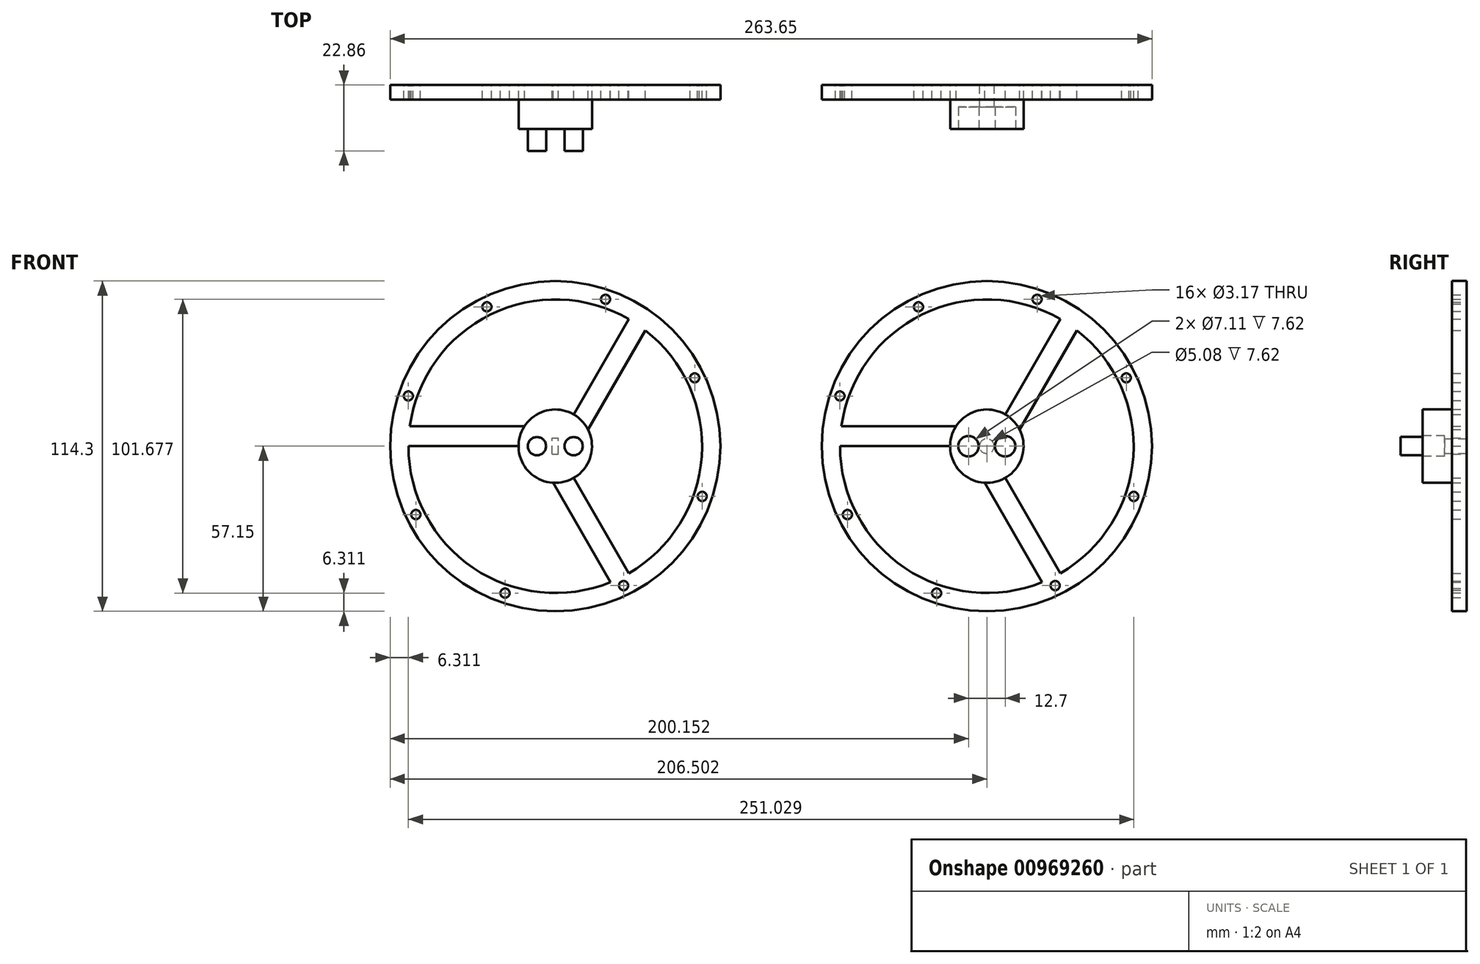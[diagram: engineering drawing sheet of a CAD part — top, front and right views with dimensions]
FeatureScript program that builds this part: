
annotation { "Feature Type Name" : "Feature", "Feature Type Description" : "" }
export const myFeature = defineFeature(function(context is Context, id is Id, definition is map)
    precondition{}
    {
        {
            var Q0;
            Q0=qCreatedBy(makeId("Front.planeOp"),FACE);
            var sketch = newSketch(context, id + "F0", { "sketchPlane" : qUnion([Q0])});
            skCircle(sketch, "E0", {"center": v(0, 0) * mm, "radius": 50.8 * mm});
            skCircle(sketch, "E1", {"center": v(0, 0) * mm, "radius": 57.15 * mm});
            skCircle(sketch, "E2", {"center": v(0, 0) * mm, "radius": 12.7 * mm});
            skLineSegment(sketch, "E3", {"start": v(-50.8, 0) * mm, "end": v(0, 0) * mm});
            skLineSegment(sketch, "E4.bottom", {"start": v(0, 0) * mm, "end": v(-53.72, 0) * mm});
            skLineSegment(sketch, "E4.top", {"start": v(0, 6.97) * mm, "end": v(-53.72, 6.97) * mm});
            skLineSegment(sketch, "E4.left", {"start": v(0, 0) * mm, "end": v(0, 6.97) * mm});
            skLineSegment(sketch, "E4.right", {"start": v(-53.72, 0) * mm, "end": v(-53.72, 6.97) * mm});
            skLineSegment(sketch, "E5.1.0", {"start": v(0, 0) * mm, "end": v(-6.03, -3.48) * mm});
            skLineSegment(sketch, "E5.1.1", {"start": v(-6.03, -3.48) * mm, "end": v(20.83, -50) * mm});
            skLineSegment(sketch, "E5.1.2", {"start": v(0, 0) * mm, "end": v(26.86, -46.52) * mm});
            skLineSegment(sketch, "E5.1.3", {"start": v(26.86, -46.52) * mm, "end": v(20.83, -50) * mm});
            skLineSegment(sketch, "E5.2.0", {"start": v(0, 0) * mm, "end": v(6.03, -3.48) * mm});
            skLineSegment(sketch, "E5.2.1", {"start": v(6.03, -3.48) * mm, "end": v(32.9, 43.04) * mm});
            skLineSegment(sketch, "E5.2.2", {"start": v(0, 0) * mm, "end": v(26.86, 46.52) * mm});
            skLineSegment(sketch, "E5.2.3", {"start": v(26.86, 46.52) * mm, "end": v(32.9, 43.04) * mm});
            skSolve(sketch);
        }
        {
            var Q0;
            {var subQ5=sQuery(id+"F0.wireOp",EDGE,"E4.left");Q0=makeQuery(id+"F0.imprint","IMPRINT",FACE,{"disambiguationData":[TD([[makeQuery(id+"F0.imprint","IMPRINT",EDGE,{"derivedFrom":subQ5}),1.0]])]});}
            var Q1;
            {var subQ5=sQuery(id+"F0.wireOp",EDGE,"E4.left");Q1=makeQuery(id+"F0.imprint","IMPRINT",FACE,{"disambiguationData":[TD([[makeQuery(id+"F0.imprint","IMPRINT",EDGE,{"derivedFrom":subQ5}),-1.0]])]});}
            var Q2;
            {var subQ5=sQuery(id+"F0.wireOp",EDGE,"E5.2.0");Q2=makeQuery(id+"F0.imprint","IMPRINT",FACE,{"disambiguationData":[TD([[makeQuery(id+"F0.imprint","IMPRINT",EDGE,{"derivedFrom":subQ5}),1.0]])]});}
            var Q3;
            {var subQ0=sQuery(id+"F0.wireOp",EDGE,"E5.2.2");var subQ1=sQuery(id+"F0.wireOp",EDGE,"E0");var subQ2=makeQuery(id+"F0.imprint","INTERSECT",VERTEX,{"derivedFrom":[subQ1,subQ0]});Q3=makeQuery(id+"F0.imprint","IMPRINT",FACE,{"disambiguationData":[TD([[makeQuery(id+"F0.imprint","IMPRINT",EDGE,{"disambiguationData":[TD([[subQ2,1.0]])],"derivedFrom":subQ1}),1.0]])]});}
            var Q4;
            {var subQ5=sQuery(id+"F0.wireOp",EDGE,"E5.2.0");Q4=makeQuery(id+"F0.imprint","IMPRINT",FACE,{"disambiguationData":[TD([[makeQuery(id+"F0.imprint","IMPRINT",EDGE,{"derivedFrom":subQ5}),-1.0]])]});}
            var Q5;
            {var subQ5=sQuery(id+"F0.wireOp",EDGE,"E5.1.0");Q5=makeQuery(id+"F0.imprint","IMPRINT",FACE,{"disambiguationData":[TD([[makeQuery(id+"F0.imprint","IMPRINT",EDGE,{"derivedFrom":subQ5}),1.0]])]});}
            var Q6;
            {var subQ5=sQuery(id+"F0.wireOp",EDGE,"E5.1.0");Q6=makeQuery(id+"F0.imprint","IMPRINT",FACE,{"disambiguationData":[TD([[makeQuery(id+"F0.imprint","IMPRINT",EDGE,{"derivedFrom":subQ5}),-1.0]])]});}
            var Q7;
            {var subQ0=sQuery(id+"F0.wireOp",EDGE,"E5.1.1");var subQ1=sQuery(id+"F0.wireOp",EDGE,"E0");var subQ2=makeQuery(id+"F0.imprint","INTERSECT",VERTEX,{"derivedFrom":[subQ1,subQ0]});Q7=makeQuery(id+"F0.imprint","IMPRINT",FACE,{"disambiguationData":[TD([[makeQuery(id+"F0.imprint","IMPRINT",EDGE,{"disambiguationData":[TD([[subQ2,-1.0]])],"derivedFrom":subQ1}),1.0]])]});}
            var Q8;
            {var subQ0=sQuery(id+"F0.wireOp",EDGE,"E4.top");var subQ1=sQuery(id+"F0.wireOp",EDGE,"E0");var subQ2=makeQuery(id+"F0.imprint","INTERSECT",VERTEX,{"derivedFrom":[subQ1,subQ0]});Q8=makeQuery(id+"F0.imprint","IMPRINT",FACE,{"disambiguationData":[TD([[makeQuery(id+"F0.imprint","IMPRINT",EDGE,{"disambiguationData":[TD([[subQ2,-1.0]])],"derivedFrom":subQ1}),1.0]])]});}
            var Q9;
            {var subQ5=sQuery(id+"F0.wireOp",EDGE,"E5.2.3");Q9=makeQuery(id+"F0.imprint","IMPRINT",FACE,{"disambiguationData":[TD([[makeQuery(id+"F0.imprint","IMPRINT",EDGE,{"derivedFrom":subQ5}),-1.0]])]});}
            var Q10;
            {var subQ5=sQuery(id+"F0.wireOp",EDGE,"E5.1.3");Q10=makeQuery(id+"F0.imprint","IMPRINT",FACE,{"disambiguationData":[TD([[makeQuery(id+"F0.imprint","IMPRINT",EDGE,{"derivedFrom":subQ5}),-1.0]])]});}
            var Q11;
            {var subQ5=sQuery(id+"F0.wireOp",EDGE,"E4.right");Q11=makeQuery(id+"F0.imprint","IMPRINT",FACE,{"disambiguationData":[TD([[makeQuery(id+"F0.imprint","IMPRINT",EDGE,{"derivedFrom":subQ5}),-1.0]])]});}
            var Q12;
            Q12=makeQuery(id+"F0.imprint","IMPRINT",FACE,{"disambiguationData":[TD([[makeQuery(id+"F0.imprint","IMPRINT",EDGE,{"derivedFrom":sQuery(id+"F0.wireOp",EDGE,"E1")}),1.0]])]});
            extrude(context, id + "F1", {"entities" : qUnion([Q0, Q1, Q2, Q3, Q4, Q5, Q6, Q7, Q8, Q9, Q10, Q11, Q12]), "depth" : 5.08 * mm, "offsetDistance" : 25.4 * mm});
        }
        {
            var Q0;
            Q0=makeQuery(id+"F1.opExtrude","CAP_FACE",FACE,{"disambiguationData":[OSD([sQuery(id+"F0.wireOp",EDGE,"E0"),sQuery(id+"F0.wireOp",EDGE,"E1"),sQuery(id+"F0.wireOp",EDGE,"E2"),sQuery(id+"F0.wireOp",EDGE,"E4.bottom"),sQuery(id+"F0.wireOp",EDGE,"E4.top"),sQuery(id+"F0.wireOp",EDGE,"E5.1.1"),sQuery(id+"F0.wireOp",EDGE,"E5.1.2"),sQuery(id+"F0.wireOp",EDGE,"E5.2.1"),sQuery(id+"F0.wireOp",EDGE,"E5.2.2")])],"isStart":false});
            var sketch = newSketch(context, id + "F2", { "sketchPlane" : qUnion([Q0])});
            skCircle(sketch, "E6", {"center": v(0, 0) * mm, "radius": 12.7 * mm});
            skSolve(sketch);
        }
        {
            var Q0;
            {var subQ0=sQuery(id+"F2.wireOp",EDGE,"E6");var subQ4=makeQuery(id+"F2.imprint","INTERSECT",VERTEX,{"derivedFrom":[makeQuery(id+"F1.opExtrude","CAP_EDGE",EDGE,{"disambiguationData":[OSD([sQuery(id+"F0.wireOp",EDGE,"E5.2.2")])],"isStart":false}),subQ0]});Q0=makeQuery(id+"F2.imprint","IMPRINT",FACE,{"disambiguationData":[TD([[makeQuery(id+"F2.imprint","IMPRINT",EDGE,{"disambiguationData":[TD([[subQ4,1.0]])],"derivedFrom":subQ0}),1.0]])]});}
            extrude(context, id + "F3", {"entities" : qUnion([Q0]), "operationType" : NewBodyOperationType.ADD, "depth" : 10.16 * mm, "offsetDistance" : 25.4 * mm});
        }
        {
            var Q0;
            Q0=makeQuery(id+"F1.opExtrude","CAP_FACE",FACE,{"disambiguationData":[OSD([sQuery(id+"F0.wireOp",EDGE,"E0"),sQuery(id+"F0.wireOp",EDGE,"E1"),sQuery(id+"F0.wireOp",EDGE,"E2"),sQuery(id+"F0.wireOp",EDGE,"E4.bottom"),sQuery(id+"F0.wireOp",EDGE,"E4.top"),sQuery(id+"F0.wireOp",EDGE,"E5.1.1"),sQuery(id+"F0.wireOp",EDGE,"E5.1.2"),sQuery(id+"F0.wireOp",EDGE,"E5.2.1"),sQuery(id+"F0.wireOp",EDGE,"E5.2.2")])],"isStart":true});
            var sketch = newSketch(context, id + "F4", { "sketchPlane" : qUnion([Q0])});
            skCircle(sketch, "E7", {"center": v(-23.65, -48.24) * mm, "radius": 1.59 * mm});
            skCircle(sketch, "E8.1.0", {"center": v(17.39, -50.84) * mm, "radius": 1.59 * mm});
            skCircle(sketch, "E8.2.0", {"center": v(48.24, -23.65) * mm, "radius": 1.59 * mm});
            skCircle(sketch, "E8.3.0", {"center": v(50.84, 17.39) * mm, "radius": 1.59 * mm});
            skCircle(sketch, "E8.4.0", {"center": v(23.65, 48.24) * mm, "radius": 1.59 * mm});
            skCircle(sketch, "E8.5.0", {"center": v(-17.39, 50.84) * mm, "radius": 1.59 * mm});
            skCircle(sketch, "E8.6.0", {"center": v(-48.24, 23.65) * mm, "radius": 1.59 * mm});
            skCircle(sketch, "E8.7.0", {"center": v(-50.84, -17.39) * mm, "radius": 1.59 * mm});
            skPoint(sketch, "E8.center", {"position": v(0, 0) * mm});
            skSolve(sketch);
        }
        {
            var Q0;
            Q0=makeQuery(id+"F4.imprint","IMPRINT",FACE,{"disambiguationData":[TD([[makeQuery(id+"F4.imprint","IMPRINT",EDGE,{"derivedFrom":sQuery(id+"F4.wireOp",EDGE,"E7")}),1.0]])]});
            var Q1;
            Q1=makeQuery(id+"F4.imprint","IMPRINT",FACE,{"disambiguationData":[TD([[makeQuery(id+"F4.imprint","IMPRINT",EDGE,{"derivedFrom":sQuery(id+"F4.wireOp",EDGE,"E8.7.0")}),1.0]])]});
            var Q2;
            Q2=makeQuery(id+"F4.imprint","IMPRINT",FACE,{"disambiguationData":[TD([[makeQuery(id+"F4.imprint","IMPRINT",EDGE,{"derivedFrom":sQuery(id+"F4.wireOp",EDGE,"E8.6.0")}),1.0]])]});
            var Q3;
            Q3=makeQuery(id+"F4.imprint","IMPRINT",FACE,{"disambiguationData":[TD([[makeQuery(id+"F4.imprint","IMPRINT",EDGE,{"derivedFrom":sQuery(id+"F4.wireOp",EDGE,"E8.5.0")}),1.0]])]});
            var Q4;
            Q4=makeQuery(id+"F4.imprint","IMPRINT",FACE,{"disambiguationData":[TD([[makeQuery(id+"F4.imprint","IMPRINT",EDGE,{"derivedFrom":sQuery(id+"F4.wireOp",EDGE,"E8.4.0")}),1.0]])]});
            var Q5;
            Q5=makeQuery(id+"F4.imprint","IMPRINT",FACE,{"disambiguationData":[TD([[makeQuery(id+"F4.imprint","IMPRINT",EDGE,{"derivedFrom":sQuery(id+"F4.wireOp",EDGE,"E8.3.0")}),1.0]])]});
            var Q6;
            Q6=makeQuery(id+"F4.imprint","IMPRINT",FACE,{"disambiguationData":[TD([[makeQuery(id+"F4.imprint","IMPRINT",EDGE,{"derivedFrom":sQuery(id+"F4.wireOp",EDGE,"E8.2.0")}),1.0]])]});
            var Q7;
            Q7=makeQuery(id+"F4.imprint","IMPRINT",FACE,{"disambiguationData":[TD([[makeQuery(id+"F4.imprint","IMPRINT",EDGE,{"derivedFrom":sQuery(id+"F4.wireOp",EDGE,"E8.1.0")}),1.0]])]});
            extrude(context, id + "F5", {"entities" : qUnion([Q0, Q1, Q2, Q3, Q4, Q5, Q6, Q7]), "operationType" : NewBodyOperationType.REMOVE, "oppositeDirection" : true, "depth" : 25.4 * mm, "offsetDistance" : 25.4 * mm});
        }
        {
            var Q0;
            Q0=makeQuery(id+"F3.opExtrude","CAP_FACE",FACE,{"disambiguationData":[OSD([sQuery(id+"F2.wireOp",EDGE,"E6")])],"isStart":false});
            var sketch = newSketch(context, id + "F6", { "sketchPlane" : qUnion([Q0])});
            skPoint(sketch, "E9.center", {"position": v(0, 0) * mm});
            skLineSegment(sketch, "E10", {"start": v(0, 0) * mm, "end": v(6.35, 0) * mm});
            skCircle(sketch, "E11", {"center": v(6.35, 0) * mm, "radius": 3.18 * mm});
            skCircle(sketch, "E12.1.1", {"center": v(-6.35, 0) * mm, "radius": 3.17 * mm});
            skSolve(sketch);
        }
        {
            var Q0;
            Q0=makeQuery(id+"F1.opExtrude","SWEPT_BODY",BODY,{"disambiguationData":[OSD([sQuery(id+"F0.wireOp",EDGE,"E0"),sQuery(id+"F0.wireOp",EDGE,"E1"),sQuery(id+"F0.wireOp",EDGE,"E2"),sQuery(id+"F0.wireOp",EDGE,"E4.bottom"),sQuery(id+"F0.wireOp",EDGE,"E4.top"),sQuery(id+"F0.wireOp",EDGE,"E5.1.1"),sQuery(id+"F0.wireOp",EDGE,"E5.1.2"),sQuery(id+"F0.wireOp",EDGE,"E5.2.1"),sQuery(id+"F0.wireOp",EDGE,"E5.2.2")])]});
            transform(context, id + "F7", {"entities" : qUnion([Q0]), "transformType" : TransformType.TRANSLATION_3D, "dx" : 177.3 * mm, "dy" : 0 * mm, "dz" : 0 * mm, "makeCopy" : true});
        }
        {
            var Q0;
            Q0=makeQuery(id+"F6.imprint","IMPRINT",FACE,{"disambiguationData":[TD([[makeQuery(id+"F6.imprint","IMPRINT",EDGE,{"derivedFrom":sQuery(id+"F6.wireOp",EDGE,"E12.1.1")}),1.0]])]});
            var Q1;
            Q1=makeQuery(id+"F6.imprint","IMPRINT",FACE,{"disambiguationData":[TD([[makeQuery(id+"F6.imprint","IMPRINT",EDGE,{"derivedFrom":sQuery(id+"F6.wireOp",EDGE,"E12.2.1")}),1.0]])]});
            var Q2;
            Q2=makeQuery(id+"F6.imprint","IMPRINT",FACE,{"disambiguationData":[TD([[makeQuery(id+"F6.imprint","IMPRINT",EDGE,{"derivedFrom":sQuery(id+"F6.wireOp",EDGE,"E11")}),1.0]])]});
            extrude(context, id + "F8", {"entities" : qUnion([Q0, Q1, Q2]), "operationType" : NewBodyOperationType.ADD, "depth" : 7.62 * mm, "offsetDistance" : 25.4 * mm});
        }
        {
            var Q0;
            Q0=makeQuery(id+"F7.opPattern","COPY",BODY,{"derivedFrom":makeQuery(id+"F1.opExtrude","SWEPT_BODY",BODY,{"disambiguationData":[OSD([sQuery(id+"F0.wireOp",EDGE,"E0"),sQuery(id+"F0.wireOp",EDGE,"E1"),sQuery(id+"F0.wireOp",EDGE,"E2"),sQuery(id+"F0.wireOp",EDGE,"E4.bottom"),sQuery(id+"F0.wireOp",EDGE,"E4.top"),sQuery(id+"F0.wireOp",EDGE,"E5.1.1"),sQuery(id+"F0.wireOp",EDGE,"E5.1.2"),sQuery(id+"F0.wireOp",EDGE,"E5.2.1"),sQuery(id+"F0.wireOp",EDGE,"E5.2.2")])]}),"instanceName":"1"});
            deleteBodies(context, id + "F9", {"entities" : qUnion([Q0])});
        }
        {
            var Q0;
            Q0=makeQuery(id+"F1.opExtrude","SWEPT_BODY",BODY,{"disambiguationData":[OSD([sQuery(id+"F0.wireOp",EDGE,"E0"),sQuery(id+"F0.wireOp",EDGE,"E1"),sQuery(id+"F0.wireOp",EDGE,"E2"),sQuery(id+"F0.wireOp",EDGE,"E4.bottom"),sQuery(id+"F0.wireOp",EDGE,"E4.top"),sQuery(id+"F0.wireOp",EDGE,"E5.1.1"),sQuery(id+"F0.wireOp",EDGE,"E5.1.2"),sQuery(id+"F0.wireOp",EDGE,"E5.2.1"),sQuery(id+"F0.wireOp",EDGE,"E5.2.2")])]});
            transform(context, id + "F10", {"entities" : qUnion([Q0]), "transformType" : TransformType.TRANSLATION_3D, "dx" : 149.35 * mm, "dy" : 0 * mm, "dz" : 0 * mm, "makeCopy" : true});
        }
        {
            var Q0;
            Q0=makeQuery(id+"F10.opPattern","COPY",FACE,{"derivedFrom":makeQuery(id+"F1.opExtrude","CAP_FACE",FACE,{"disambiguationData":[OSD([sQuery(id+"F0.wireOp",EDGE,"E0"),sQuery(id+"F0.wireOp",EDGE,"E1"),sQuery(id+"F0.wireOp",EDGE,"E2"),sQuery(id+"F0.wireOp",EDGE,"E4.bottom"),sQuery(id+"F0.wireOp",EDGE,"E4.top"),sQuery(id+"F0.wireOp",EDGE,"E5.1.1"),sQuery(id+"F0.wireOp",EDGE,"E5.1.2"),sQuery(id+"F0.wireOp",EDGE,"E5.2.1"),sQuery(id+"F0.wireOp",EDGE,"E5.2.2")])],"isStart":true}),"instanceName":"1"});
            var sketch = newSketch(context, id + "F11", { "sketchPlane" : qUnion([Q0])});
            skCircle(sketch, "E13", {"center": v(-149.35, 0) * mm, "radius": 2.54 * mm});
            skSolve(sketch);
        }
        {
            var Q0;
            Q0=makeQuery(id+"F11.imprint","IMPRINT",FACE,{"disambiguationData":[TD([[makeQuery(id+"F11.imprint","IMPRINT",EDGE,{"derivedFrom":sQuery(id+"F11.wireOp",EDGE,"E13")}),1.0]])]});
            extrude(context, id + "F12", {"entities" : qUnion([Q0]), "operationType" : NewBodyOperationType.REMOVE, "oppositeDirection" : true, "depth" : 7.62 * mm, "offsetDistance" : 25.4 * mm});
        }
        {
            var Q0;
            Q0=makeQuery(id+"F1.opExtrude","CAP_FACE",FACE,{"disambiguationData":[OSD([sQuery(id+"F0.wireOp",EDGE,"E0"),sQuery(id+"F0.wireOp",EDGE,"E1"),sQuery(id+"F0.wireOp",EDGE,"E2"),sQuery(id+"F0.wireOp",EDGE,"E4.bottom"),sQuery(id+"F0.wireOp",EDGE,"E4.top"),sQuery(id+"F0.wireOp",EDGE,"E5.1.1"),sQuery(id+"F0.wireOp",EDGE,"E5.1.2"),sQuery(id+"F0.wireOp",EDGE,"E5.2.1"),sQuery(id+"F0.wireOp",EDGE,"E5.2.2")])],"isStart":true});
            var sketch = newSketch(context, id + "F13", { "sketchPlane" : qUnion([Q0])});
            skLineSegment(sketch, "E14.bottom", {"start": v(1.08, -2.8) * mm, "end": v(-1.08, -2.8) * mm});
            skLineSegment(sketch, "E14.top", {"start": v(1.08, 2.8) * mm, "end": v(-1.08, 2.8) * mm});
            skLineSegment(sketch, "E14.left", {"start": v(1.08, -2.8) * mm, "end": v(1.08, 2.8) * mm});
            skLineSegment(sketch, "E14.right", {"start": v(-1.08, -2.8) * mm, "end": v(-1.08, 2.8) * mm});
            skPoint(sketch, "E14.middle", {"position": v(0, 0) * mm});
            skSolve(sketch);
        }
        {
            var Q0;
            Q0=makeQuery(id+"F13.imprint","IMPRINT",FACE,{"disambiguationData":[TD([[makeQuery(id+"F13.imprint","IMPRINT",EDGE,{"derivedFrom":sQuery(id+"F13.wireOp",EDGE,"E14.bottom")}),-1.0]])]});
            extrude(context, id + "F14", {"entities" : qUnion([Q0]), "operationType" : NewBodyOperationType.REMOVE, "oppositeDirection" : true, "depth" : 5.08 * mm, "offsetDistance" : 25.4 * mm});
        }
        {
            var Q0;
            Q0=makeQuery(id+"F10.opPattern","COPY",FACE,{"derivedFrom":makeQuery(id+"F8.opExtrude","CAP_FACE",FACE,{"disambiguationData":[OSD([sQuery(id+"F6.wireOp",EDGE,"E11")])],"isStart":false}),"instanceName":"1"});
            var sketch = newSketch(context, id + "F15", { "sketchPlane" : qUnion([Q0])});
            skCircle(sketch, "E15", {"center": v(155.7, 0) * mm, "radius": 3.56 * mm});
            skCircle(sketch, "E16.1.0", {"center": v(143, 0) * mm, "radius": 3.56 * mm});
            skPoint(sketch, "E16.center", {"position": v(149.35, 0) * mm});
            skSolve(sketch);
        }
        {
            var Q0;
            Q0=makeQuery(id+"F15.imprint","IMPRINT",FACE,{"disambiguationData":[TD([[makeQuery(id+"F15.imprint","IMPRINT",EDGE,{"derivedFrom":sQuery(id+"F15.wireOp",EDGE,"E16.1.0")}),1.0]])]});
            var Q1;
            Q1=makeQuery(id+"F15.imprint","IMPRINT",FACE,{"disambiguationData":[TD([[makeQuery(id+"F15.imprint","IMPRINT",EDGE,{"derivedFrom":sQuery(id+"F15.wireOp",EDGE,"E15")}),1.0]])]});
            var Q2;
            Q2=makeQuery(id+"F15.imprint","IMPRINT",FACE,{"disambiguationData":[TD([[makeQuery(id+"F15.imprint","IMPRINT",EDGE,{"derivedFrom":makeQuery(id+"F10.opPattern","COPY",EDGE,{"derivedFrom":makeQuery(id+"F8.opExtrude","CAP_EDGE",EDGE,{"disambiguationData":[OSD([sQuery(id+"F6.wireOp",EDGE,"E11")])],"isStart":false}),"instanceName":"1"})}),1.0]])]});
            extrude(context, id + "F16", {"entities" : qUnion([Q0, Q1, Q2]), "operationType" : NewBodyOperationType.REMOVE, "oppositeDirection" : true, "depth" : 15.24 * mm, "offsetDistance" : 25.4 * mm});
        }
    });
